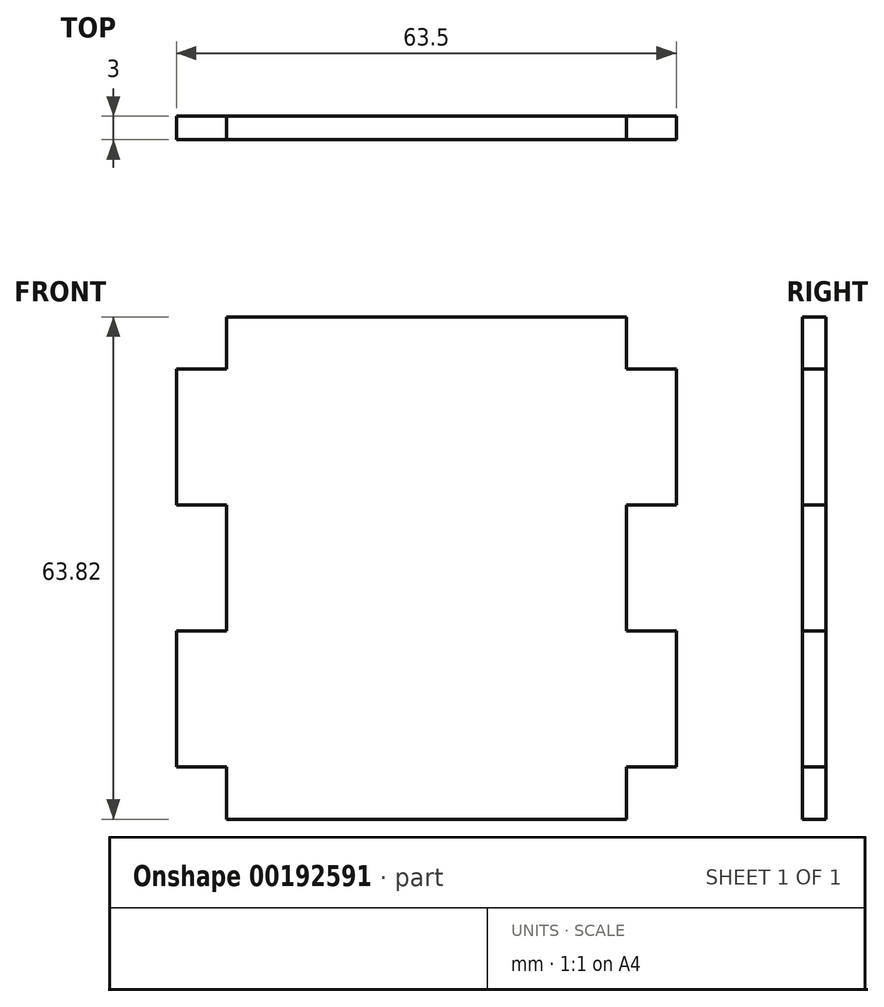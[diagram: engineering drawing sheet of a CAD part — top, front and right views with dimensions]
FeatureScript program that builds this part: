
annotation { "Feature Type Name" : "Feature", "Feature Type Description" : "" }
export const myFeature = defineFeature(function(context is Context, id is Id, definition is map)
    precondition{}
    {
        {
            var Q0;
            Q0=qCreatedBy(makeId("Front.planeOp"),FACE);
            var sketch = newSketch(context, id + "F0", { "sketchPlane" : qUnion([Q0])});
            skLineSegment(sketch, "E0.bottom", {"start": v(25.4, -31.91) * mm, "end": v(-25.4, -31.91) * mm});
            skLineSegment(sketch, "E0.top", {"start": v(25.4, 31.91) * mm, "end": v(-25.4, 31.91) * mm});
            skLineSegment(sketch, "E0.left", {"start": v(25.4, -31.91) * mm, "end": v(25.4, 31.91) * mm});
            skLineSegment(sketch, "E0.right", {"start": v(-25.4, -31.91) * mm, "end": v(-25.4, 31.91) * mm});
            skPoint(sketch, "E0.middle", {"position": v(0, 0) * mm});
            skLineSegment(sketch, "E1.bottom", {"start": v(-18.29, 8) * mm, "end": v(-21.6, 8) * mm});
            skLineSegment(sketch, "E1.top", {"start": v(-18.29, 25.27) * mm, "end": v(-21.6, 25.27) * mm});
            skLineSegment(sketch, "E1.left", {"start": v(-18.29, 8) * mm, "end": v(-18.29, 25.27) * mm});
            skLineSegment(sketch, "E1.right", {"start": v(-21.6, 8) * mm, "end": v(-21.6, 25.27) * mm});
            skPoint(sketch, "E1.middle", {"position": v(-19.94, 16.64) * mm});
            skLineSegment(sketch, "E2.MirrorCS", {"start": v(18.29, 8) * mm, "end": v(18.29, 25.27) * mm});
            skLineSegment(sketch, "E3.MirrorCS", {"start": v(21.6, 8) * mm, "end": v(21.6, 25.27) * mm});
            skLineSegment(sketch, "E4.MirrorCS", {"start": v(18.29, 8) * mm, "end": v(21.6, 8) * mm});
            skLineSegment(sketch, "E5.MirrorCS", {"start": v(18.29, 25.27) * mm, "end": v(21.6, 25.27) * mm});
            skLineSegment(sketch, "E6.MirrorCS", {"start": v(18.29, -8) * mm, "end": v(21.6, -8) * mm});
            skLineSegment(sketch, "E7.MirrorCS", {"start": v(21.6, -8) * mm, "end": v(21.6, -25.27) * mm});
            skLineSegment(sketch, "E8.MirrorCS", {"start": v(18.29, -8) * mm, "end": v(18.29, -25.27) * mm});
            skLineSegment(sketch, "E9.MirrorCS", {"start": v(18.29, -25.27) * mm, "end": v(21.6, -25.27) * mm});
            skLineSegment(sketch, "E10.MirrorCS", {"start": v(-18.29, -8) * mm, "end": v(-18.29, -25.27) * mm});
            skLineSegment(sketch, "E11.MirrorCS", {"start": v(-21.6, -8) * mm, "end": v(-21.6, -25.27) * mm});
            skLineSegment(sketch, "E12.MirrorCS", {"start": v(-18.29, -8) * mm, "end": v(-21.6, -8) * mm});
            skLineSegment(sketch, "E13.MirrorCS", {"start": v(-18.29, -25.27) * mm, "end": v(-21.6, -25.27) * mm});
            skLineSegment(sketch, "E14", {"start": v(31.75, 8) * mm, "end": v(31.75, 25.27) * mm});
            skLineSegment(sketch, "E15.trimOffspring", {"start": v(25.4, 8) * mm, "end": v(31.75, 8) * mm});
            skLineSegment(sketch, "E16.trimOffspring", {"start": v(25.4, 25.27) * mm, "end": v(31.75, 25.27) * mm});
            skLineSegment(sketch, "E17.MirrorCS", {"start": v(-25.4, 8) * mm, "end": v(-31.75, 8) * mm});
            skLineSegment(sketch, "E18.MirrorCS", {"start": v(-31.75, 8) * mm, "end": v(-31.75, 25.27) * mm});
            skLineSegment(sketch, "E19.MirrorCS", {"start": v(-25.4, 25.27) * mm, "end": v(-31.75, 25.27) * mm});
            skLineSegment(sketch, "E20.MirrorCS", {"start": v(25.4, -8) * mm, "end": v(31.75, -8) * mm});
            skLineSegment(sketch, "E21.MirrorCS", {"start": v(31.75, -8) * mm, "end": v(31.75, -25.27) * mm});
            skLineSegment(sketch, "E22.MirrorCS", {"start": v(25.4, -25.27) * mm, "end": v(31.75, -25.27) * mm});
            skLineSegment(sketch, "E23.MirrorCS", {"start": v(-25.4, -8) * mm, "end": v(-31.75, -8) * mm});
            skLineSegment(sketch, "E24.MirrorCS", {"start": v(-31.75, -8) * mm, "end": v(-31.75, -25.27) * mm});
            skLineSegment(sketch, "E25.MirrorCS", {"start": v(-25.4, -25.27) * mm, "end": v(-31.75, -25.27) * mm});
            skSolve(sketch);
        }
        {
            var Q0;
            Q0=makeQuery(id+"F0.imprint","IMPRINT",FACE,{"disambiguationData":[TD([[makeQuery(id+"F0.imprint","IMPRINT",EDGE,{"derivedFrom":sQuery(id+"F0.wireOp",EDGE,"E1.top")}),1.0]])]});
            var Q1;
            {var subQ8=sQuery(id+"F0.wireOp",EDGE,"E0.bottom");Q1=makeQuery(id+"F0.imprint","IMPRINT",FACE,{"disambiguationData":[TD([[makeQuery(id+"F0.imprint","IMPRINT",EDGE,{"derivedFrom":subQ8}),-1.0]])]});}
            var Q2;
            Q2=makeQuery(id+"F0.imprint","IMPRINT",FACE,{"disambiguationData":[TD([[makeQuery(id+"F0.imprint","IMPRINT",EDGE,{"derivedFrom":sQuery(id+"F0.wireOp",EDGE,"E2.MirrorCS")}),-1.0]])]});
            var Q3;
            Q3=makeQuery(id+"F0.imprint","IMPRINT",FACE,{"disambiguationData":[TD([[makeQuery(id+"F0.imprint","IMPRINT",EDGE,{"derivedFrom":sQuery(id+"F0.wireOp",EDGE,"E6.MirrorCS")}),-1.0]])]});
            var Q4;
            Q4=makeQuery(id+"F0.imprint","IMPRINT",FACE,{"disambiguationData":[TD([[makeQuery(id+"F0.imprint","IMPRINT",EDGE,{"derivedFrom":sQuery(id+"F0.wireOp",EDGE,"E10.MirrorCS")}),-1.0]])]});
            var Q5;
            {var subQ0=sQuery(id+"F0.wireOp",EDGE,"E23.MirrorCS");Q5=makeQuery(id+"F0.imprint","IMPRINT",FACE,{"disambiguationData":[TD([[makeQuery(id+"F0.imprint","IMPRINT",EDGE,{"derivedFrom":subQ0}),1.0]])]});}
            var Q6;
            {var subQ0=sQuery(id+"F0.wireOp",EDGE,"E17.MirrorCS");Q6=makeQuery(id+"F0.imprint","IMPRINT",FACE,{"disambiguationData":[TD([[makeQuery(id+"F0.imprint","IMPRINT",EDGE,{"derivedFrom":subQ0}),-1.0]])]});}
            var Q7;
            Q7=makeQuery(id+"F0.imprint","IMPRINT",FACE,{"disambiguationData":[TD([[makeQuery(id+"F0.imprint","IMPRINT",EDGE,{"derivedFrom":sQuery(id+"F0.wireOp",EDGE,"E14")}),1.0]])]});
            var Q8;
            {var subQ0=sQuery(id+"F0.wireOp",EDGE,"E20.MirrorCS");Q8=makeQuery(id+"F0.imprint","IMPRINT",FACE,{"disambiguationData":[TD([[makeQuery(id+"F0.imprint","IMPRINT",EDGE,{"derivedFrom":subQ0}),-1.0]])]});}
            extrude(context, id + "F1", {"entities" : qUnion([Q0, Q1, Q2, Q3, Q4, Q5, Q6, Q7, Q8]), "depth" : 3 * mm});
        }
    });
